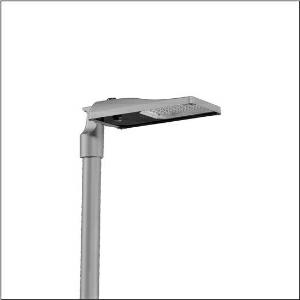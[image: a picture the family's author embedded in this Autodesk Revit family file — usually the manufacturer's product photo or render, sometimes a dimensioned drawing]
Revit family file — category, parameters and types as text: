
# Revit family: streetlight_sl_31_mini___st1_0a_5xh2d3at08ja_abb8
name_source: partatom
category: Lighting Fixtures
units: mm (PartAtom-declared; Revit-internal decimal feet)

## family parameters
Cut with Voids When Loaded = No
Host = Face
Light Source = No
Part Type = Normal
Room Calculation Point = No
Round Connector Dimension = Use Diameter
Shared = No

## types (1)
- --- (1 x LED, 12270 lm, 82.5 W, 3000K)
    Apparent Load = 83 VA
    CIE Flux Codes = 40 73 97 100 100
    Color Rendering = 70
    Color Temperature = 3000K
    Default Elevation = 1800 mm
    Description = Streetlight SL 31 mini D4i mast luminaire for post-top, side-entry; light control with lens of PMMA; light distribution: ST1.0a, direct asymmetric distribution, for standard-compliant lighting for roads and squares; LED: luminous flux: 12.270lm, light colour: 730, colour temperature: 3000K; luminous efficacy: 148,7lm/W; control: pre-setting: logarithmic dimming characteristic, flexible luminous flux parameterisation, time-dependent luminous flux control, constant luminous flux control, power reduction, intelligent temperature release in ECG and LED module, overheat protection; luminaire housing, of diecast aluminium, Siteco® metallic grey (DB 702S), corrosivity category C5 high according to DIN EN ISO 12944; cover of toughened safety glass, transparent, mast flange of diecast aluminium, Siteco® metallic grey (DB 702S), spigot size: 76/60mm, mast flange included unmounted; with cable H07RN-F 2x 1.5mm², cable length: 10,5m, connection cable pre-assembled; mains connection: 220..240V, AC, 50/60Hz; power consumption (at start of service life): 82,5W / (at end of service life): 90,1W / (with reduced operation 50%): 36,8W; protection rating (complete): IP66; insulation class (complete): insulation class II (safety insulation); impact resistance: IK09; certification: CE, ENEC, ENEC+, VDE, UKCA, ZD4i; permissible operating ambient temperature for outdoor applications: -40..+50°C; packaging unit: 1 piece

Light Distribution: ST1.0a
    Height = 76 mm
    Lamp = 1 x LED
    Lamp Light Flux = 12270 lm
    Lamp Power = 82.5 W
    Lamp count = 1
    Length = 547 mm
    Luminous efficacy = 149 lm/W
    Manufacturer = Siteco
    ModVariant = No
    Model = 5XH2D3AT08JA
    Number of Poles = 1
    OnlyDefault = Yes
    Power Factor = 1
    Product Name = Streetlight SL 31 mini | ST1.0a
    Product group = mast luminaire | pylon top
    ProductGroupID = 6100
    Protection Class = Protection class II
    Protection Degree = IP 66
    RLX_Detail_Level = 1
    RLX_Emergency_Light_Flux = 0 lm
    RLX_Emergency_Type = 0
    RLX_Emergency_Type_DB = No
    RlxData = <blob elided: 39837 chars, md5=0b26b6a0>
    Socket = socket
    Standby Power = 0 W
    System Light Flux = 12270 lm
    System Power = 83 W
    Type Comments = factory setting: luminous flux: 100 % | dim-lin: 254 | 870 mA
    Type Image = l_1300332.jpg
    URL = http://relux.com
    VarID = @adj_050726
    Voltage = 0 V
    Weight = 0.00 kg
    Width = 265 mm

## geometry (parser evidence)
native form markers: Blend x4, Sweep x11
no freeform markers — native parametric forms only
